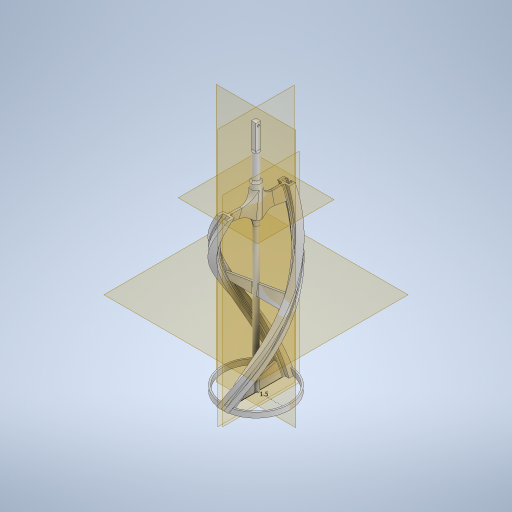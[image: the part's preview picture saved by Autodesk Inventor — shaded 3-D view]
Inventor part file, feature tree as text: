
AUTODESK INVENTOR PART (.ipt)
format: ipt  version: 2023.2 (Build 272271030, 271C)  size: 1,092,608 bytes
history: native  units: in
note: dims shown in document units (in); Inventor stores cm internally (conversion verified against a paired STEP export)
features: other x13, sketch x10, extrude x5, fillet x5, plane x4, hole x1
ambient origin geometry x8: Origin, YZ Plane, XZ Plane, XY Plane, X Axis, Y Axis, Z Axis, Center Point
bodies: Solid1 (feature_tree)
feature tree (38):
  other  "Main Helix"
  extrude  "Center Shaft"  Depth=0.1299in
  other  "Midplane"
  other  "Buttom Support"
  plane  "Work Plane5"
  other  "Work Point5"
  other  "Work Point6"
  other  "Work Point7"
  other  "Work Point8"
  other  "Top Support"
  other  "Work Point1"
  other  "Work Point4"
  other  "Work Point3"
  other  "Work Point2"
  other  "Mid Support"
  extrude  "Bottom Ring"  Depth=0.0787in
  fillet  "Fillet1"  Radius=0.0315in
  extrude  "Shaft Coupler"  Depth=0.3937in
  plane  "Work Plane7"
  fillet  "Fillet6"  Radius=0.1969in
  fillet  "Fillet8"  Radius=0.3937in
  extrude  "Shaft"  Depth=0.2362in
  fillet  "Fillet9"  Radius=1.4764in
  extrude  "Gear Square"  Depth=0.1398in
  fillet  "Fillet10"  Radius=0.0394in
  hole  "Hole3"  [1 undecoded]
  plane  "Work Plane10"
  plane  "Work Plane11"
  sketch  "Sketch1"  dims[d0=4.0in]
  sketch  "Sketch7"  dims[d3=0.0in d4=90.0deg d5=90.0deg d6=0.0in d7=0.0in d39=0.1299in]
  sketch  "Sketch9"  dims[d41=0.0551in d42=0.0787in d45=0.0315in]
  sketch  "Sketch10"  dims[d46=0.0787in d47=0.0787in d49=0.1969in d50=0.3937in d51=0.0in]
  sketch  "Sketch12"  dims[d52=12.5984in d53=0.4199in d54=0.0984in d55=0.0in d56=90.0deg d57=90.0deg d58=0.0in d59=0.0in d60=0.2362in d61=1.4764in]
  sketch  "Sketch13"  dims[d62=0.0591in]
  sketch  "Sketch15"  dims[d64=12.5984in d65=0.4199in d66=0.0984in d67=0.0in d68=90.0deg d69=90.0deg d70=0.0in d71=0.0in d72=0.1398in d73=0.0394in]
  sketch  "Sketch19"  dims[d76=12.5984in d77=0.4199in d78=0.3937in d79=0.0in d80=90.0deg d81=90.0deg d82=0.0in d83=0.0in d84=0.0591in]
  sketch  "Sketch20"  dims[d85=0.1969in d86=0.0in]
  sketch  "Sketch21"  dims[d87=0.0394in d88=0.0591in d91=0.375in d92=1.1811in d93=0.0in d110=0.0551in d111=0.3937in d122=0.7874in d123=0.2461in d124=0.9843in d125=0.0in d126=0.0787in d127=0.9843in d128=0.0in d129=0.0787in d130=0.1181in d131=0.0894in d132=0.224in d133=0.1575in d134=0.0787in d135=90.0deg d136=0.315in d137=0.8108in d112=0.0in d113=0.0in]
note: 1 required parameter value undecoded (feature->parameter linkage not recoverable at this tier; creation-order binding heuristic only, values carry confidence <= 0.55)
